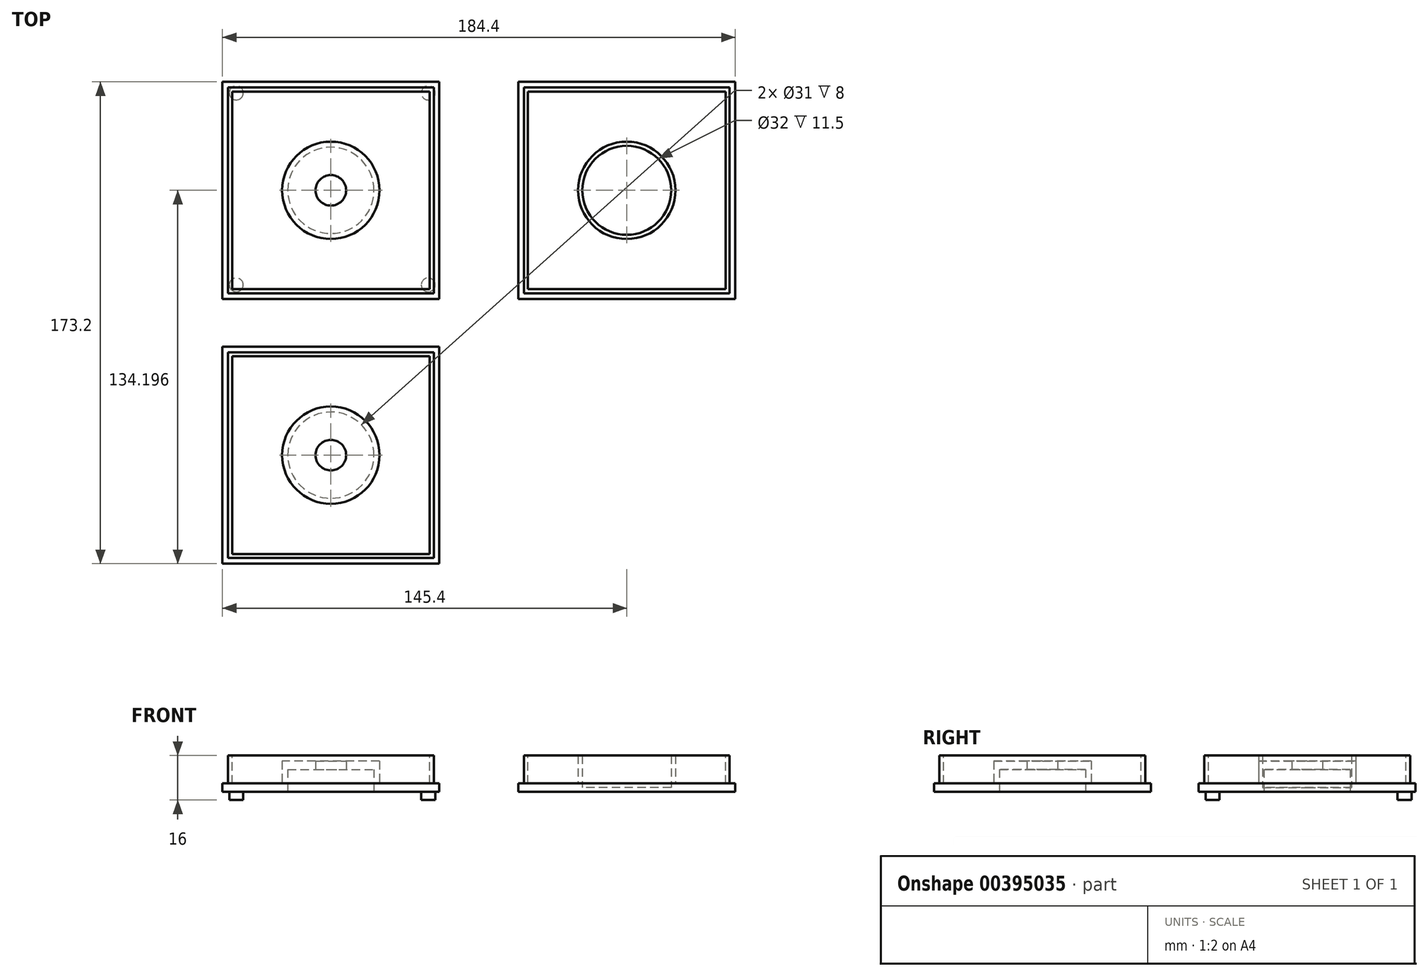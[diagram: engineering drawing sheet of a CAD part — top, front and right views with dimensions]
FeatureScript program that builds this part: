
annotation { "Feature Type Name" : "Feature", "Feature Type Description" : "" }
export const myFeature = defineFeature(function(context is Context, id is Id, definition is map)
    precondition{}
    {
        {
            var Q0;
            Q0=qCreatedBy(makeId("Top.planeOp"),FACE);
            var sketch = newSketch(context, id + "F0", { "sketchPlane" : qUnion([Q0])});
            skLineSegment(sketch, "E0.bottom", {"start": v(-49.84, -57.73) * mm, "end": v(28.16, -57.73) * mm});
            skLineSegment(sketch, "E0.top", {"start": v(-49.84, 20.27) * mm, "end": v(28.16, 20.27) * mm});
            skLineSegment(sketch, "E0.left", {"start": v(-49.84, -57.73) * mm, "end": v(-49.84, 20.27) * mm});
            skLineSegment(sketch, "E0.right", {"start": v(28.16, -57.73) * mm, "end": v(28.16, 20.27) * mm});
            skPoint(sketch, "E1", {"position": v(-10.84, -18.73) * mm});
            skLineSegment(sketch, "E2.bottom", {"start": v(28.16, 20.27) * mm, "end": v(26.16, 20.27) * mm});
            skLineSegment(sketch, "E2.left", {"start": v(28.16, 20.27) * mm, "end": v(28.16, 18.27) * mm});
            skLineSegment(sketch, "E3.bottom", {"start": v(26.16, 18.27) * mm, "end": v(-47.84, 18.27) * mm});
            skLineSegment(sketch, "E3.top", {"start": v(26.16, -55.73) * mm, "end": v(-47.84, -55.73) * mm});
            skLineSegment(sketch, "E3.left", {"start": v(26.16, 18.27) * mm, "end": v(26.16, -55.73) * mm});
            skLineSegment(sketch, "E3.right", {"start": v(-47.84, 18.27) * mm, "end": v(-47.84, -55.73) * mm});
            skSolve(sketch);
        }
        {
            var Q0;
            Q0=makeQuery(id+"F0.imprint","IMPRINT",FACE,{"disambiguationData":[TD([[makeQuery(id+"F0.imprint","IMPRINT",EDGE,{"derivedFrom":sQuery(id+"F0.wireOp",EDGE,"E3.bottom")}),1.0]])]});
            extrude(context, id + "F1", {"entities" : qUnion([Q0]), "depth" : 10 * mm});
        }
        {
            var Q0;
            Q0=makeQuery(id+"F0.imprint","IMPRINT",FACE,{"disambiguationData":[TD([[makeQuery(id+"F0.imprint","IMPRINT",EDGE,{"derivedFrom":sQuery(id+"F0.wireOp",EDGE,"E0.bottom")}),1.0]])]});
            var Q1;
            Q1=makeQuery(id+"F0.imprint","IMPRINT",FACE,{"disambiguationData":[TD([[makeQuery(id+"F0.imprint","IMPRINT",EDGE,{"derivedFrom":sQuery(id+"F0.wireOp",EDGE,"E3.bottom")}),1.0]])]});
            extrude(context, id + "F2", {"entities" : qUnion([Q0, Q1]), "operationType" : NewBodyOperationType.ADD, "oppositeDirection" : true, "depth" : 3 * mm});
        }
        {
            var Q0;
            Q0=makeQuery(id+"F1.opExtrude","CAP_FACE",FACE,{"disambiguationData":[OSD([sQuery(id+"F0.wireOp",EDGE,"E3.bottom"),sQuery(id+"F0.wireOp",EDGE,"E3.top"),sQuery(id+"F0.wireOp",EDGE,"E3.left"),sQuery(id+"F0.wireOp",EDGE,"E3.right")])],"isStart":false});
            var sketch = newSketch(context, id + "F3", { "sketchPlane" : qUnion([Q0])});
            skLineSegment(sketch, "E4.bottom", {"start": v(26.16, 18.27) * mm, "end": v(24.66, 18.27) * mm});
            skLineSegment(sketch, "E4.left", {"start": v(26.16, 18.27) * mm, "end": v(26.16, 16.77) * mm});
            skLineSegment(sketch, "E5.bottom", {"start": v(-47.84, -55.73) * mm, "end": v(-46.34, -55.73) * mm});
            skLineSegment(sketch, "E5.left", {"start": v(-47.84, -55.73) * mm, "end": v(-47.84, -54.23) * mm});
            skLineSegment(sketch, "E6.bottom", {"start": v(-46.34, -54.23) * mm, "end": v(24.66, -54.23) * mm});
            skLineSegment(sketch, "E6.top", {"start": v(-46.34, 16.77) * mm, "end": v(24.66, 16.77) * mm});
            skLineSegment(sketch, "E6.left", {"start": v(-46.34, -54.23) * mm, "end": v(-46.34, 16.77) * mm});
            skLineSegment(sketch, "E6.right", {"start": v(24.66, -54.23) * mm, "end": v(24.66, 16.77) * mm});
            skSolve(sketch);
        }
        {
            var Q0;
            Q0=makeQuery(id+"F3.imprint","IMPRINT",FACE,{"disambiguationData":[TD([[makeQuery(id+"F3.imprint","IMPRINT",EDGE,{"derivedFrom":sQuery(id+"F3.wireOp",EDGE,"E6.bottom")}),1.0]])]});
            extrude(context, id + "F4", {"entities" : qUnion([Q0]), "operationType" : NewBodyOperationType.REMOVE, "oppositeDirection" : true, "depth" : 10 * mm});
        }
        {
            var Q0;
            Q0=makeQuery(id+"F4.boolean.opBoolean","COPY",FACE,{"derivedFrom":makeQuery(id+"F4.opExtrude","CAP_FACE",FACE,{"disambiguationData":[OSD([sQuery(id+"F3.wireOp",EDGE,"E6.bottom"),sQuery(id+"F3.wireOp",EDGE,"E6.top"),sQuery(id+"F3.wireOp",EDGE,"E6.left"),sQuery(id+"F3.wireOp",EDGE,"E6.right")])],"isStart":false})});
            var sketch = newSketch(context, id + "F5", { "sketchPlane" : qUnion([Q0])});
            skPoint(sketch, "E7", {"position": v(-10.84, -18.73) * mm});
            skCircle(sketch, "E8", {"center": v(-10.84, -18.73) * mm, "radius": 17.5 * mm});
            skSolve(sketch);
        }
        {
            var Q0;
            Q0=makeQuery(id+"F5.imprint","IMPRINT",FACE,{"disambiguationData":[TD([[makeQuery(id+"F5.imprint","IMPRINT",EDGE,{"derivedFrom":sQuery(id+"F5.wireOp",EDGE,"E8")}),1.0]])]});
            extrude(context, id + "F6", {"entities" : qUnion([Q0]), "operationType" : NewBodyOperationType.ADD, "depth" : 10 * mm});
        }
        {
            var Q0;
            Q0=makeQuery(id+"F1.opExtrude","SWEPT_BODY",BODY,{"disambiguationData":[OSD([sQuery(id+"F0.wireOp",EDGE,"E3.bottom"),sQuery(id+"F0.wireOp",EDGE,"E3.top"),sQuery(id+"F0.wireOp",EDGE,"E3.left"),sQuery(id+"F0.wireOp",EDGE,"E3.right")])]});
            transform(context, id + "F7", {"entities" : qUnion([Q0]), "transformType" : TransformType.TRANSLATION_3D, "dx" : -106.4 * mm, "dy" : 0 * mm, "dz" : 0 * mm, "makeCopy" : true});
        }
        {
            var Q0;
            Q0=makeQuery(id+"F6.opExtrude","CAP_FACE",FACE,{"disambiguationData":[OSD([sQuery(id+"F5.wireOp",EDGE,"E8")])],"isStart":false});
            shell(context, id + "F8", {"entities" : qUnion([Q0]), "thickness" : 1.5 * mm});
        }
        {
            var Q0;
            Q0=makeQuery(id+"F7.opPattern","COPY",FACE,{"derivedFrom":makeQuery(id+"F6.opExtrude","CAP_FACE",FACE,{"disambiguationData":[OSD([sQuery(id+"F5.wireOp",EDGE,"E8")])],"isStart":false}),"instanceName":"1"});
            shell(context, id + "F9", {"entities" : qUnion([Q0]), "thickness" : 2.5 * mm});
        }
        {
            var Q0;
            Q0=makeQuery(id+"F7.opPattern","COPY",FACE,{"derivedFrom":makeQuery(id+"F6.opExtrude","CAP_FACE",FACE,{"disambiguationData":[OSD([sQuery(id+"F5.wireOp",EDGE,"E8")])],"isStart":false}),"instanceName":"1"});
            var sketch = newSketch(context, id + "F10", { "sketchPlane" : qUnion([Q0])});
            skSolve(sketch);
        }
        {
            var Q0;
            {var subQ0=sQuery(id+"F5.wireOp",EDGE,"E8");Q0=makeQuery(id+"F10.imprint","IMPRINT",FACE,{"disambiguationData":[TD([[makeQuery(id+"F10.imprint","IMPRINT",EDGE,{"derivedFrom":makeQuery(id+"F7.opPattern","COPY",EDGE,{"derivedFrom":makeQuery(id+"F6.opExtrude","CAP_EDGE",EDGE,{"disambiguationData":[OSD([subQ0])],"isStart":false}),"instanceName":"1"})}),1.0]])]});}
            extrude(context, id + "F11", {"entities" : qUnion([Q0]), "operationType" : NewBodyOperationType.REMOVE, "depth" : -2 * mm});
        }
        {
            var Q0;
            Q0=makeQuery(id+"F9.opShell","OFFSET_FACE",FACE,{"disambiguationData":[OSD([sQuery(id+"F0.wireOp",EDGE,"E0.bottom"),sQuery(id+"F0.wireOp",EDGE,"E0.top"),sQuery(id+"F0.wireOp",EDGE,"E0.left"),sQuery(id+"F0.wireOp",EDGE,"E0.right"),sQuery(id+"F0.wireOp",EDGE,"E2.bottom"),sQuery(id+"F0.wireOp",EDGE,"E2.left")])]});
            extrude(context, id + "F12", {"entities" : qUnion([Q0]), "operationType" : NewBodyOperationType.ADD, "depth" : 8.5 * mm});
        }
        {
            var Q0;
            Q0=makeQuery(id+"F7.opPattern","COPY",FACE,{"derivedFrom":makeQuery(id+"F2.opExtrude","CAP_FACE",FACE,{"disambiguationData":[OSD([sQuery(id+"F0.wireOp",EDGE,"E0.bottom"),sQuery(id+"F0.wireOp",EDGE,"E0.top"),sQuery(id+"F0.wireOp",EDGE,"E0.left"),sQuery(id+"F0.wireOp",EDGE,"E0.right"),sQuery(id+"F0.wireOp",EDGE,"E2.bottom"),sQuery(id+"F0.wireOp",EDGE,"E2.left")])],"isStart":false}),"instanceName":"1"});
            var sketch = newSketch(context, id + "F13", { "sketchPlane" : qUnion([Q0])});
            skPoint(sketch, "E9", {"position": v(-117.24, 18.73) * mm});
            skCircle(sketch, "E10", {"center": v(-117.24, 18.73) * mm, "radius": 16 * mm});
            skSolve(sketch);
        }
        {
            var Q0;
            Q0=sQuery(id+"F13.wireOp",VERTEX,"E9");
            var Q1;
            Q1=makeQuery(id+"F7.opPattern","COPY",BODY,{"derivedFrom":makeQuery(id+"F1.opExtrude","SWEPT_BODY",BODY,{"disambiguationData":[OSD([sQuery(id+"F0.wireOp",EDGE,"E3.bottom"),sQuery(id+"F0.wireOp",EDGE,"E3.top"),sQuery(id+"F0.wireOp",EDGE,"E3.left"),sQuery(id+"F0.wireOp",EDGE,"E3.right")])]}),"instanceName":"1"});
            hole(context, id + "F14", {"style" : HoleStyle.C_SINK, "endStyle" : HoleEndStyle.THROUGH, "holeDiameter" : 11 * mm, "cSinkDiameter" : 11 * mm, "cSinkAngle" : 90 * degree, "isTappedThrough" : true, "tappedDepth" : 12 * mm, "tapClearance" : 3, "startFromSketch" : true, "locations" : qUnion([Q0]), "scope" : qUnion([Q1])});
        }
        {
            var Q0;
            Q0=makeQuery(id+"F7.opPattern","COPY",FACE,{"derivedFrom":makeQuery(id+"F2.opExtrude","CAP_FACE",FACE,{"disambiguationData":[OSD([sQuery(id+"F0.wireOp",EDGE,"E0.bottom"),sQuery(id+"F0.wireOp",EDGE,"E0.top"),sQuery(id+"F0.wireOp",EDGE,"E0.left"),sQuery(id+"F0.wireOp",EDGE,"E0.right"),sQuery(id+"F0.wireOp",EDGE,"E2.bottom"),sQuery(id+"F0.wireOp",EDGE,"E2.left")])],"isStart":false}),"instanceName":"1"});
            var sketch = newSketch(context, id + "F15", { "sketchPlane" : qUnion([Q0])});
            skPoint(sketch, "E11", {"position": v(-117.24, 18.73) * mm});
            skCircle(sketch, "E12", {"center": v(-117.24, 18.73) * mm, "radius": 15.5 * mm});
            skSolve(sketch);
        }
        {
            var Q0;
            Q0=makeQuery(id+"F15.imprint","IMPRINT",FACE,{"disambiguationData":[TD([[makeQuery(id+"F15.imprint","IMPRINT",EDGE,{"derivedFrom":sQuery(id+"F15.wireOp",EDGE,"E12")}),1.0]])]});
            extrude(context, id + "F16", {"entities" : qUnion([Q0]), "operationType" : NewBodyOperationType.REMOVE, "oppositeDirection" : true, "depth" : 8 * mm});
        }
        {
            var Q0;
            Q0=makeQuery(id+"F7.opPattern","COPY",FACE,{"derivedFrom":makeQuery(id+"F2.opExtrude","CAP_FACE",FACE,{"disambiguationData":[OSD([sQuery(id+"F0.wireOp",EDGE,"E0.bottom"),sQuery(id+"F0.wireOp",EDGE,"E0.top"),sQuery(id+"F0.wireOp",EDGE,"E0.left"),sQuery(id+"F0.wireOp",EDGE,"E0.right"),sQuery(id+"F0.wireOp",EDGE,"E2.bottom"),sQuery(id+"F0.wireOp",EDGE,"E2.left")])],"isStart":false}),"instanceName":"1"});
            var sketch = newSketch(context, id + "F17", { "sketchPlane" : qUnion([Q0])});
            skLineSegment(sketch, "E13.bottom", {"start": v(-78.24, -20.27) * mm, "end": v(-82.24, -20.27) * mm});
            skLineSegment(sketch, "E13.left", {"start": v(-78.24, -20.27) * mm, "end": v(-78.24, -16.27) * mm});
            skPoint(sketch, "E14", {"position": v(-82.24, -16.27) * mm});
            skCircle(sketch, "E15", {"center": v(-82.24, -16.27) * mm, "radius": 2.5 * mm});
            skLineSegment(sketch, "E16.bottom", {"start": v(-156.24, 57.73) * mm, "end": v(-151.24, 57.73) * mm});
            skLineSegment(sketch, "E16.left", {"start": v(-156.24, 57.73) * mm, "end": v(-156.24, 52.73) * mm});
            skCircle(sketch, "E17", {"center": v(-151.24, 52.73) * mm, "radius": 2.5 * mm});
            skCircle(sketch, "E18", {"center": v(-151.24, -16.27) * mm, "radius": 2.5 * mm});
            skCircle(sketch, "E19", {"center": v(-82.24, 52.73) * mm, "radius": 2.5 * mm});
            skSolve(sketch);
        }
        {
            var Q0;
            Q0=makeQuery(id+"F7.opPattern","COPY",BODY,{"derivedFrom":makeQuery(id+"F1.opExtrude","SWEPT_BODY",BODY,{"disambiguationData":[OSD([sQuery(id+"F0.wireOp",EDGE,"E3.bottom"),sQuery(id+"F0.wireOp",EDGE,"E3.top"),sQuery(id+"F0.wireOp",EDGE,"E3.left"),sQuery(id+"F0.wireOp",EDGE,"E3.right")])]}),"instanceName":"1"});
            transform(context, id + "F18", {"entities" : qUnion([Q0]), "transformType" : TransformType.TRANSLATION_3D, "dx" : 0 * mm, "dy" : -95.2 * mm, "dz" : 0 * mm, "makeCopy" : true});
        }
        {
            var Q0;
            Q0=makeQuery(id+"F17.imprint","IMPRINT",FACE,{"disambiguationData":[TD([[makeQuery(id+"F17.imprint","IMPRINT",EDGE,{"derivedFrom":sQuery(id+"F17.wireOp",EDGE,"E17")}),1.0]])]});
            var Q1;
            Q1=makeQuery(id+"F17.imprint","IMPRINT",FACE,{"disambiguationData":[TD([[makeQuery(id+"F17.imprint","IMPRINT",EDGE,{"derivedFrom":sQuery(id+"F17.wireOp",EDGE,"E18")}),1.0]])]});
            var Q2;
            Q2=makeQuery(id+"F17.imprint","IMPRINT",FACE,{"disambiguationData":[TD([[makeQuery(id+"F17.imprint","IMPRINT",EDGE,{"derivedFrom":sQuery(id+"F17.wireOp",EDGE,"E15")}),1.0]])]});
            var Q3;
            Q3=makeQuery(id+"F17.imprint","IMPRINT",FACE,{"disambiguationData":[TD([[makeQuery(id+"F17.imprint","IMPRINT",EDGE,{"derivedFrom":sQuery(id+"F17.wireOp",EDGE,"E19")}),1.0]])]});
            extrude(context, id + "F19", {"entities" : qUnion([Q0, Q1, Q2, Q3]), "operationType" : NewBodyOperationType.ADD, "depth" : 3 * mm});
        }
    });
